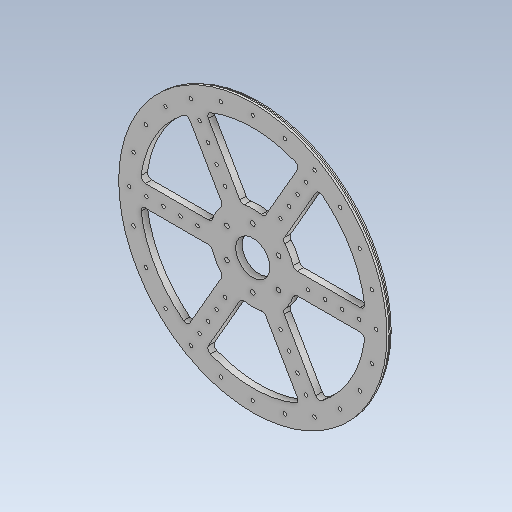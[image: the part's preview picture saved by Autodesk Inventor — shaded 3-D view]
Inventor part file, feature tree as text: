
AUTODESK INVENTOR PART (.ipt)
format: ipt  version: 2020 (Build 240168000, 168)  size: 281,088 bytes
history: native  units: in
note: dims shown in document units (in); Inventor stores cm internally (conversion verified against a paired STEP export)
features: sketch x4, other x3
ambient origin geometry x8: Origin, YZ Plane, XZ Plane, XY Plane, X Axis, Y Axis, Z Axis, Center Point
bodies: Solid1 (feature_tree)
feature tree (7):
  other  "IndexerWheelV2.ipt"
  other  "Solid1::IndexerWheelV2.ipt"
  other  "TaggingFeature1"
  sketch  "Sketch1"  dims[d0=0.3937in]
  sketch  "Sketch2"
  sketch  "Sketch3"
  sketch  "Sketch5"
